# Revit family: RN 90030 Optifitt-Serra-Nippel
name_source: partatom
category: Rohrformteile
units: mm (PartAtom-declared; Revit-internal decimal feet)

## family parameters
Arbeitsebenenbasiert = Nein
Beim Laden mit Abzugskörper schneiden = Nein
Bemaßung runder Anschluss = Durchmesser verwenden
Gemeinsam genutzt = Nein
Immer vertikal = Ja
Teiletyp = Nicht definiert

## types (8) — shared parameters
1.010.00.2 Blattnummer der Richtlinie = 29
1.010.00.3 Ausgabedatum (Monat) der Richtlinie = 201308
1.010.00.4 Herstellername = R. Nussbaum AG
1.010.00.5 Revisionsdatum der Datei = 20190521
1.010.00.6 Webadresse des Herstellers = http://www.nussbaum.ch
1.100.00.4 Produktbezeichnung = Versorgung
1.110.00.2 Index = 3
1.110.00.4 Produktbezeichnung = Optifitt-Serra
1.960/3L.00.8 Link (URL) = https://www.nussbaum.ch
29.700.00.4 Produktname = Optifitt-Serra-Nippel
29.700.00.5 Produktkennung = 2
29.700.00.6 Querschnittsform = 1
29.700.00.7 Nennweitensystem = DN
29.700.00.8 Nenndrucksystem = PN
29.710.02.4 Nenndruck = 16
29.710.02.5 max. zul. Überdruck [hPa] = 1600
29.710.02.7 max. zul. Dauer-Betriebsdruck [hPa] = 1600
29.710.02.9 max. zul. Dauer-Betriebstemperatur [°C] = 90
Connector Visibility = Nein
EnclosingSpace Visibility = Nein
Hersteller = R. Nussbaum AG
URL = https://www.nussbaum.ch

## per-type parameters (varying)
- DN=50: 1.800.00.3 TGA-Nummer=01900300000000000000000000000000000000000000000017000000000000000008; 1.800.00.4 Kommentarfeld=90030.09, Optifitt-Serra-Nippel, DN=50, L=47; 1.810.00.3 Hersteller-Bestellnummer=90030.09; 1.810.00.4 DATANORM-Nummer=90030.09; 1.810.00.6 GTIN-Nummer=7612945033949; 29.710.02.10 Formstück-Gewicht [kg]=0.214; 29.710.02.3 Benennung=Optifitt-Serra-Nippel, DN=50, L=47; CONNECTOR0_DIAMETER_dX_0r=50 mm; CONNECTOR0_dX_01=24 mm; CONNECTOR0_ref_dX=24 mm; CONNECTOR1_DIAMETER_dX_0r=50 mm; CONNECTOR1_dX_00=23 mm; CONNECTOR1_dX_01=47 mm; CONNECTOR1_ref_dX=23 mm; CONNECTOR1_ref_dX2=47 mm; Modell=90030.09; R. Nussbaum AG 90030.02 de Visibility=Nein; R. Nussbaum AG 90030.03 de Visibility=Nein; R. Nussbaum AG 90030.04 de Visibility=Nein; R. Nussbaum AG 90030.05 de Visibility=Nein; R. Nussbaum AG 90030.06 de Visibility=Nein; R. Nussbaum AG 90030.07 de Visibility=Nein; R. Nussbaum AG 90030.08 de Visibility=Nein; R. Nussbaum AG 90030.09 de Visibility=Ja; Typenkommentare=Optifitt-Serra-Nippel DN=50
- DN=40: 1.800.00.3 TGA-Nummer=01900300000000000000000000000000000000000000000017000000000000000007; 1.800.00.4 Kommentarfeld=90030.08, Optifitt-Serra-Nippel, DN=40, L=42; 1.810.00.3 Hersteller-Bestellnummer=90030.08; 1.810.00.4 DATANORM-Nummer=90030.08; 1.810.00.6 GTIN-Nummer=7612945033932; 29.710.02.10 Formstück-Gewicht [kg]=0.157; 29.710.02.3 Benennung=Optifitt-Serra-Nippel, DN=40, L=42; CONNECTOR0_DIAMETER_dX_0r=40 mm; CONNECTOR0_dX_01=19 mm; CONNECTOR0_ref_dX=19 mm; CONNECTOR1_DIAMETER_dX_0r=40 mm; CONNECTOR1_dX_00=23 mm; CONNECTOR1_dX_01=42 mm; CONNECTOR1_ref_dX=23 mm; CONNECTOR1_ref_dX2=42 mm; Modell=90030.08; R. Nussbaum AG 90030.02 de Visibility=Nein; R. Nussbaum AG 90030.03 de Visibility=Nein; R. Nussbaum AG 90030.04 de Visibility=Nein; R. Nussbaum AG 90030.05 de Visibility=Nein; R. Nussbaum AG 90030.06 de Visibility=Nein; R. Nussbaum AG 90030.07 de Visibility=Nein; R. Nussbaum AG 90030.08 de Visibility=Ja; R. Nussbaum AG 90030.09 de Visibility=Nein; Typenkommentare=Optifitt-Serra-Nippel DN=40
- DN=32: 1.800.00.3 TGA-Nummer=01900300000000000000000000000000000000000000000017000000000000000006; 1.800.00.4 Kommentarfeld=90030.07, Optifitt-Serra-Nippel, DN=32, L=37; 1.810.00.3 Hersteller-Bestellnummer=90030.07; 1.810.00.4 DATANORM-Nummer=90030.07; 1.810.00.6 GTIN-Nummer=7612945033925; 29.710.02.10 Formstück-Gewicht [kg]=0.121; 29.710.02.3 Benennung=Optifitt-Serra-Nippel, DN=32, L=37; CONNECTOR0_DIAMETER_dX_0r=32 mm; CONNECTOR0_dX_01=19 mm; CONNECTOR0_ref_dX=19 mm; CONNECTOR1_DIAMETER_dX_0r=32 mm; CONNECTOR1_dX_00=18 mm; CONNECTOR1_dX_01=37 mm  [stored 0.121391 ft]; CONNECTOR1_ref_dX=18 mm; CONNECTOR1_ref_dX2=37 mm  [stored 0.121391 ft]; Modell=90030.07; R. Nussbaum AG 90030.02 de Visibility=Nein; R. Nussbaum AG 90030.03 de Visibility=Nein; R. Nussbaum AG 90030.04 de Visibility=Nein; R. Nussbaum AG 90030.05 de Visibility=Nein; R. Nussbaum AG 90030.06 de Visibility=Nein; R. Nussbaum AG 90030.07 de Visibility=Ja; R. Nussbaum AG 90030.08 de Visibility=Nein; R. Nussbaum AG 90030.09 de Visibility=Nein; Typenkommentare=Optifitt-Serra-Nippel DN=32
- DN=25: 1.800.00.3 TGA-Nummer=01900300000000000000000000000000000000000000000017000000000000000005; 1.800.00.4 Kommentarfeld=90030.06, Optifitt-Serra-Nippel, DN=25, L=33; 1.810.00.3 Hersteller-Bestellnummer=90030.06; 1.810.00.4 DATANORM-Nummer=90030.06; 1.810.00.6 GTIN-Nummer=7612945033918; 29.710.02.10 Formstück-Gewicht [kg]=0.078; 29.710.02.3 Benennung=Optifitt-Serra-Nippel, DN=25, L=33; CONNECTOR0_DIAMETER_dX_0r=25 mm  [stored 0.082021 ft]; CONNECTOR0_dX_01=17 mm; CONNECTOR0_ref_dX=17 mm; CONNECTOR1_DIAMETER_dX_0r=25 mm  [stored 0.082021 ft]; CONNECTOR1_dX_00=16 mm; CONNECTOR1_dX_01=33 mm; CONNECTOR1_ref_dX=16 mm; CONNECTOR1_ref_dX2=33 mm; Modell=90030.06; R. Nussbaum AG 90030.02 de Visibility=Nein; R. Nussbaum AG 90030.03 de Visibility=Nein; R. Nussbaum AG 90030.04 de Visibility=Nein; R. Nussbaum AG 90030.05 de Visibility=Nein; R. Nussbaum AG 90030.06 de Visibility=Ja; R. Nussbaum AG 90030.07 de Visibility=Nein; R. Nussbaum AG 90030.08 de Visibility=Nein; R. Nussbaum AG 90030.09 de Visibility=Nein; Typenkommentare=Optifitt-Serra-Nippel DN=25
- DN=20: 1.800.00.3 TGA-Nummer=01900300000000000000000000000000000000000000000017000000000000000004; 1.800.00.4 Kommentarfeld=90030.05, Optifitt-Serra-Nippel, DN=20, L=26; 1.810.00.3 Hersteller-Bestellnummer=90030.05; 1.810.00.4 DATANORM-Nummer=90030.05; 1.810.00.6 GTIN-Nummer=7612945033901; 29.710.02.10 Formstück-Gewicht [kg]=0.04; 29.710.02.3 Benennung=Optifitt-Serra-Nippel, DN=20, L=26; CONNECTOR0_DIAMETER_dX_0r=20 mm; CONNECTOR0_dX_01=15 mm; CONNECTOR0_ref_dX=15 mm; CONNECTOR1_DIAMETER_dX_0r=20 mm; CONNECTOR1_dX_00=11 mm; CONNECTOR1_dX_01=26 mm; CONNECTOR1_ref_dX=11 mm; CONNECTOR1_ref_dX2=26 mm; Modell=90030.05; R. Nussbaum AG 90030.02 de Visibility=Nein; R. Nussbaum AG 90030.03 de Visibility=Nein; R. Nussbaum AG 90030.04 de Visibility=Nein; R. Nussbaum AG 90030.05 de Visibility=Ja; R. Nussbaum AG 90030.06 de Visibility=Nein; R. Nussbaum AG 90030.07 de Visibility=Nein; R. Nussbaum AG 90030.08 de Visibility=Nein; R. Nussbaum AG 90030.09 de Visibility=Nein; Typenkommentare=Optifitt-Serra-Nippel DN=20
- DN=15: 1.800.00.3 TGA-Nummer=01900300000000000000000000000000000000000000000017000000000000000003; 1.800.00.4 Kommentarfeld=90030.04, Optifitt-Serra-Nippel, DN=15, L=22; 1.810.00.3 Hersteller-Bestellnummer=90030.04; 1.810.00.4 DATANORM-Nummer=90030.04; 1.810.00.6 GTIN-Nummer=7612945033895; 29.710.02.10 Formstück-Gewicht [kg]=0.023; 29.710.02.3 Benennung=Optifitt-Serra-Nippel, DN=15, L=22; CONNECTOR0_DIAMETER_dX_0r=15 mm; CONNECTOR0_dX_01=13 mm; CONNECTOR0_ref_dX=13 mm; CONNECTOR1_DIAMETER_dX_0r=15 mm; CONNECTOR1_dX_00=9 mm  [stored 0.0295276 ft]; CONNECTOR1_dX_01=22 mm; CONNECTOR1_ref_dX=9 mm  [stored 0.0295276 ft]; CONNECTOR1_ref_dX2=22 mm; Modell=90030.04; R. Nussbaum AG 90030.02 de Visibility=Nein; R. Nussbaum AG 90030.03 de Visibility=Nein; R. Nussbaum AG 90030.04 de Visibility=Ja; R. Nussbaum AG 90030.05 de Visibility=Nein; R. Nussbaum AG 90030.06 de Visibility=Nein; R. Nussbaum AG 90030.07 de Visibility=Nein; R. Nussbaum AG 90030.08 de Visibility=Nein; R. Nussbaum AG 90030.09 de Visibility=Nein; Typenkommentare=Optifitt-Serra-Nippel DN=15
- DN=10: 1.800.00.3 TGA-Nummer=01900300000000000000000000000000000000000000000017000000000000000002; 1.800.00.4 Kommentarfeld=90030.03, Optifitt-Serra-Nippel, DN=10, L=20; 1.810.00.3 Hersteller-Bestellnummer=90030.03; 1.810.00.4 DATANORM-Nummer=90030.03; 1.810.00.6 GTIN-Nummer=7612945033888; 29.710.02.10 Formstück-Gewicht [kg]=0.019; 29.710.02.3 Benennung=Optifitt-Serra-Nippel, DN=10, L=20; CONNECTOR0_DIAMETER_dX_0r=10 mm  [stored 0.0328084 ft]; CONNECTOR0_dX_01=10 mm  [stored 0.0328084 ft]; CONNECTOR0_ref_dX=10 mm  [stored 0.0328084 ft]; CONNECTOR1_DIAMETER_dX_0r=10 mm  [stored 0.0328084 ft]; CONNECTOR1_dX_00=10 mm  [stored 0.0328084 ft]; CONNECTOR1_dX_01=20 mm; CONNECTOR1_ref_dX=10 mm  [stored 0.0328084 ft]; CONNECTOR1_ref_dX2=20 mm; Modell=90030.03; R. Nussbaum AG 90030.02 de Visibility=Nein; R. Nussbaum AG 90030.03 de Visibility=Ja; R. Nussbaum AG 90030.04 de Visibility=Nein; R. Nussbaum AG 90030.05 de Visibility=Nein; R. Nussbaum AG 90030.06 de Visibility=Nein; R. Nussbaum AG 90030.07 de Visibility=Nein; R. Nussbaum AG 90030.08 de Visibility=Nein; R. Nussbaum AG 90030.09 de Visibility=Nein; Typenkommentare=Optifitt-Serra-Nippel DN=10
- DN=1: 1.800.00.3 TGA-Nummer=01900300000000000000000000000000000000000000000017000000000000000001; 1.800.00.4 Kommentarfeld=90030.02, Optifitt-Serra-Nippel, DN=10, L=20; 1.810.00.3 Hersteller-Bestellnummer=90030.02; 1.810.00.4 DATANORM-Nummer=90030.02; 1.810.00.6 GTIN-Nummer=7612945033871; 29.710.02.10 Formstück-Gewicht [kg]=0.012; 29.710.02.3 Benennung=Optifitt-Serra-Nippel, DN=10, L=20; CONNECTOR0_DIAMETER_dX_0r=8 mm  [stored 0.0262467 ft]; CONNECTOR0_dX_01=10 mm  [stored 0.0328084 ft]; CONNECTOR0_ref_dX=10 mm  [stored 0.0328084 ft]; CONNECTOR1_DIAMETER_dX_0r=8 mm  [stored 0.0262467 ft]; CONNECTOR1_dX_00=10 mm  [stored 0.0328084 ft]; CONNECTOR1_dX_01=20 mm; CONNECTOR1_ref_dX=10 mm  [stored 0.0328084 ft]; CONNECTOR1_ref_dX2=20 mm; Modell=90030.02; R. Nussbaum AG 90030.02 de Visibility=Ja; R. Nussbaum AG 90030.03 de Visibility=Nein; R. Nussbaum AG 90030.04 de Visibility=Nein; R. Nussbaum AG 90030.05 de Visibility=Nein; R. Nussbaum AG 90030.06 de Visibility=Nein; R. Nussbaum AG 90030.07 de Visibility=Nein; R. Nussbaum AG 90030.08 de Visibility=Nein; R. Nussbaum AG 90030.09 de Visibility=Nein; Typenkommentare=Optifitt-Serra-Nippel DN=10

note: [stored X ft] marks values corroborated as IEEE doubles in the binary element streams (Revit-internal decimal feet)

## geometry (parser evidence)
native form markers: Sweep x2
no freeform markers — native parametric forms only
